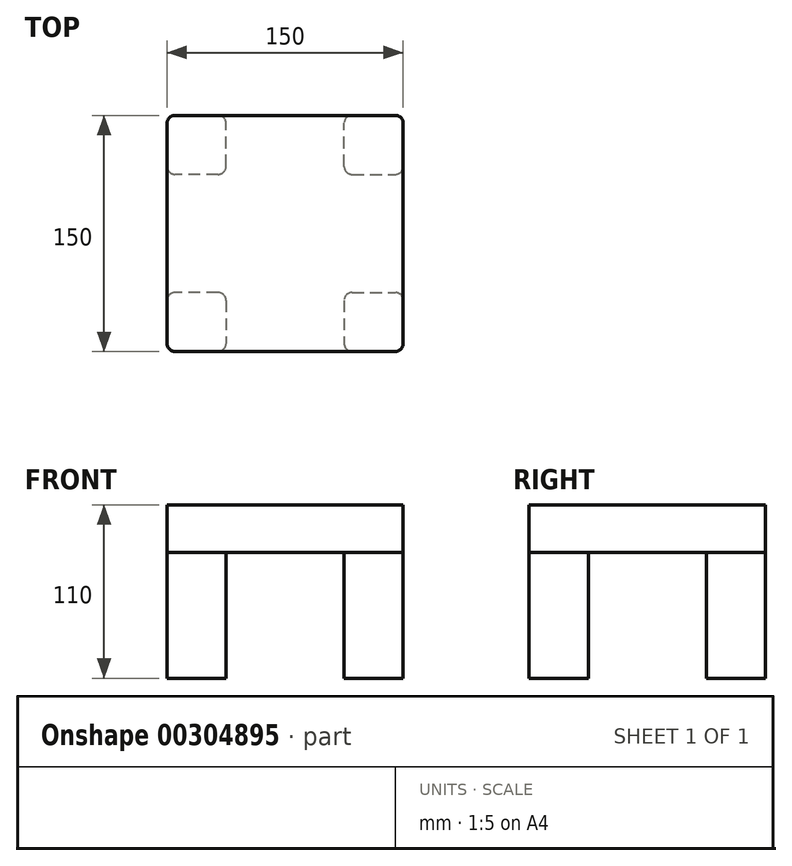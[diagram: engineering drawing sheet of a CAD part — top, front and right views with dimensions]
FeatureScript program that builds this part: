
annotation { "Feature Type Name" : "Feature", "Feature Type Description" : "" }
export const myFeature = defineFeature(function(context is Context, id is Id, definition is map)
    precondition{}
    {
        {
            var Q0;
            Q0=qCreatedBy(makeId("Top.planeOp"),FACE);
            var sketch = newSketch(context, id + "F0", { "sketchPlane" : qUnion([Q0])});
            skLineSegment(sketch, "E0.bottom", {"start": v(0, 0) * mm, "end": v(-75, 0) * mm});
            skLineSegment(sketch, "E0.top", {"start": v(0, 0) * mm, "end": v(-75, 0) * mm});
            skLineSegment(sketch, "E0.left", {"start": v(0, 0) * mm, "end": v(0, 0) * mm});
            skLineSegment(sketch, "E0.right", {"start": v(-75, 0) * mm, "end": v(-75, 0) * mm});
            skLineSegment(sketch, "E1", {"start": v(0, 0) * mm, "end": v(0, -75) * mm});
            skPoint(sketch, "E2.firstSnap0", {"position": v(-37.5, 0) * mm});
            skPoint(sketch, "E2.firstSnap1", {"position": v(0, -37.5) * mm});
            skLineSegment(sketch, "E2.bottom", {"start": v(-42.5, -37.5) * mm, "end": v(-70, -37.5) * mm});
            skLineSegment(sketch, "E2.top", {"start": v(-42.5, -75) * mm, "end": v(-70, -75) * mm});
            skLineSegment(sketch, "E2.left", {"start": v(-37.5, -42.5) * mm, "end": v(-37.5, -70) * mm});
            skLineSegment(sketch, "E2.right", {"start": v(-75, -42.5) * mm, "end": v(-75, -70) * mm});
            skLineSegment(sketch, "E3.MirrorCS", {"start": v(42.5, -37.5) * mm, "end": v(70, -37.5) * mm});
            skLineSegment(sketch, "E4.MirrorCS", {"start": v(75, -42.5) * mm, "end": v(75, -70) * mm});
            skLineSegment(sketch, "E5.MirrorCS", {"start": v(42.5, -75) * mm, "end": v(70, -75) * mm});
            skLineSegment(sketch, "E6.MirrorCS", {"start": v(37.5, -42.5) * mm, "end": v(37.5, -70) * mm});
            skLineSegment(sketch, "E7.MirrorCS", {"start": v(0, 0) * mm, "end": v(75, 0) * mm});
            skLineSegment(sketch, "E8.MirrorCS", {"start": v(-42.5, 37.5) * mm, "end": v(-70, 37.5) * mm});
            skLineSegment(sketch, "E9.MirrorCS", {"start": v(-75, 42.5) * mm, "end": v(-75, 70) * mm});
            skLineSegment(sketch, "E10.MirrorCS", {"start": v(-42.5, 75) * mm, "end": v(-70, 75) * mm});
            skLineSegment(sketch, "E11.MirrorCS", {"start": v(-37.5, 42.5) * mm, "end": v(-37.5, 70) * mm});
            skLineSegment(sketch, "E12.MirrorCS", {"start": v(37.5, 42.5) * mm, "end": v(37.5, 70) * mm});
            skLineSegment(sketch, "E13.MirrorCS", {"start": v(42.5, 37.5) * mm, "end": v(70, 37.5) * mm});
            skLineSegment(sketch, "E14.MirrorCS", {"start": v(75, 42.5) * mm, "end": v(75, 70) * mm});
            skLineSegment(sketch, "E15.MirrorCS", {"start": v(42.5, 75) * mm, "end": v(70, 75) * mm});
            skPoint(sketch, "E16.visualSharp", {"position": v(-75, -37.5) * mm});
            skArc(sketch, "E16.filletArc", {"start": v(-70, -37.5) * mm, "mid": v(-73.54, -38.96) * mm, "end": v(-75, -42.5) * mm});
            skPoint(sketch, "E17.visualSharp", {"position": v(-37.5, -37.5) * mm});
            skArc(sketch, "E17.filletArc", {"start": v(-37.5, -42.5) * mm, "mid": v(-38.96, -38.96) * mm, "end": v(-42.5, -37.5) * mm});
            skPoint(sketch, "E18.visualSharp", {"position": v(-75, -75) * mm});
            skArc(sketch, "E18.filletArc", {"start": v(-75, -70) * mm, "mid": v(-73.54, -73.54) * mm, "end": v(-70, -75) * mm});
            skPoint(sketch, "E19.visualSharp", {"position": v(-37.5, -75) * mm});
            skArc(sketch, "E19.filletArc", {"start": v(-42.5, -75) * mm, "mid": v(-38.96, -73.54) * mm, "end": v(-37.5, -70) * mm});
            skPoint(sketch, "E20.visualSharp", {"position": v(37.5, -37.5) * mm});
            skArc(sketch, "E20.filletArc", {"start": v(42.5, -37.5) * mm, "mid": v(38.96, -38.96) * mm, "end": v(37.5, -42.5) * mm});
            skPoint(sketch, "E21.visualSharp", {"position": v(75, -37.5) * mm});
            skArc(sketch, "E21.filletArc", {"start": v(75, -42.5) * mm, "mid": v(73.54, -38.96) * mm, "end": v(70, -37.5) * mm});
            skPoint(sketch, "E22.visualSharp", {"position": v(37.5, -75) * mm});
            skArc(sketch, "E22.filletArc", {"start": v(37.5, -70) * mm, "mid": v(38.96, -73.54) * mm, "end": v(42.5, -75) * mm});
            skPoint(sketch, "E23.visualSharp", {"position": v(75, -75) * mm});
            skArc(sketch, "E23.filletArc", {"start": v(70, -75) * mm, "mid": v(73.54, -73.54) * mm, "end": v(75, -70) * mm});
            skPoint(sketch, "E24.visualSharp", {"position": v(-75, 37.5) * mm});
            skArc(sketch, "E24.filletArc", {"start": v(-75, 42.5) * mm, "mid": v(-73.54, 38.96) * mm, "end": v(-70, 37.5) * mm});
            skPoint(sketch, "E25.visualSharp", {"position": v(-75, 75) * mm});
            skArc(sketch, "E25.filletArc", {"start": v(-70, 75) * mm, "mid": v(-73.54, 73.54) * mm, "end": v(-75, 70) * mm});
            skPoint(sketch, "E26.visualSharp", {"position": v(-37.5, 75) * mm});
            skArc(sketch, "E26.filletArc", {"start": v(-37.5, 70) * mm, "mid": v(-38.96, 73.54) * mm, "end": v(-42.5, 75) * mm});
            skPoint(sketch, "E27.visualSharp", {"position": v(-37.5, 37.5) * mm});
            skArc(sketch, "E27.filletArc", {"start": v(-42.5, 37.5) * mm, "mid": v(-38.96, 38.96) * mm, "end": v(-37.5, 42.5) * mm});
            skPoint(sketch, "E28.visualSharp", {"position": v(37.5, 37.5) * mm});
            skArc(sketch, "E28.filletArc", {"start": v(37.5, 42.5) * mm, "mid": v(38.96, 38.96) * mm, "end": v(42.5, 37.5) * mm});
            skPoint(sketch, "E29.visualSharp", {"position": v(37.5, 75) * mm});
            skArc(sketch, "E29.filletArc", {"start": v(42.5, 75) * mm, "mid": v(38.96, 73.54) * mm, "end": v(37.5, 70) * mm});
            skPoint(sketch, "E30.visualSharp", {"position": v(75, 75) * mm});
            skArc(sketch, "E30.filletArc", {"start": v(75, 70) * mm, "mid": v(73.54, 73.54) * mm, "end": v(70, 75) * mm});
            skPoint(sketch, "E31.visualSharp", {"position": v(75, 37.5) * mm});
            skArc(sketch, "E31.filletArc", {"start": v(70, 37.5) * mm, "mid": v(73.54, 38.96) * mm, "end": v(75, 42.5) * mm});
            skPoint(sketch, "E32.startSnap0", {"position": v(-56.25, -75) * mm});
            skPoint(sketch, "E32.startSnap1", {"position": v(-37.5, -56.25) * mm});
            skLineSegment(sketch, "E33.left", {"start": v(-56.25, -66.25) * mm, "end": v(-56.25, -66.25) * mm});
            skLineSegment(sketch, "E33.right", {"start": v(-43.75, -66.25) * mm, "end": v(-43.75, -66.25) * mm});
            skLineSegment(sketch, "E34.bottom", {"start": v(-56.25, -66.25) * mm, "end": v(-63.75, -66.25) * mm});
            skLineSegment(sketch, "E34.top", {"start": v(-48.75, -46.25) * mm, "end": v(-63.75, -46.25) * mm});
            skLineSegment(sketch, "E34.left", {"start": v(-43.75, -61.25) * mm, "end": v(-43.75, -51.25) * mm});
            skLineSegment(sketch, "E34.right", {"start": v(-68.75, -61.25) * mm, "end": v(-68.75, -51.25) * mm});
            skPoint(sketch, "E34.middle", {"position": v(-56.25, -56.25) * mm});
            skLineSegment(sketch, "E35", {"start": v(-48.75, -66.25) * mm, "end": v(-56.25, -66.25) * mm});
            skPoint(sketch, "E36.visualSharp", {"position": v(-68.75, -46.25) * mm});
            skArc(sketch, "E36.filletArc", {"start": v(-63.75, -46.25) * mm, "mid": v(-67.29, -47.71) * mm, "end": v(-68.75, -51.25) * mm});
            skPoint(sketch, "E37.visualSharp", {"position": v(-43.75, -46.25) * mm});
            skArc(sketch, "E37.filletArc", {"start": v(-43.75, -51.25) * mm, "mid": v(-45.21, -47.71) * mm, "end": v(-48.75, -46.25) * mm});
            skPoint(sketch, "E38.visualSharp", {"position": v(-43.75, -66.25) * mm});
            skArc(sketch, "E38.filletArc", {"start": v(-48.75, -66.25) * mm, "mid": v(-45.21, -64.79) * mm, "end": v(-43.75, -61.25) * mm});
            skPoint(sketch, "E39.visualSharp", {"position": v(-68.75, -66.25) * mm});
            skArc(sketch, "E39.filletArc", {"start": v(-68.75, -61.25) * mm, "mid": v(-67.29, -64.79) * mm, "end": v(-63.75, -66.25) * mm});
            skSolve(sketch);
        }
        {
            var Q0;
            Q0=makeQuery(id+"F0.imprint","IMPRINT",FACE,{"disambiguationData":[TD([[makeQuery(id+"F0.imprint","IMPRINT",EDGE,{"derivedFrom":sQuery(id+"F0.wireOp",EDGE,"E12.MirrorCS")}),-1.0]])]});
            var Q1;
            Q1=makeQuery(id+"F0.imprint","IMPRINT",FACE,{"disambiguationData":[TD([[makeQuery(id+"F0.imprint","IMPRINT",EDGE,{"derivedFrom":sQuery(id+"F0.wireOp",EDGE,"E8.MirrorCS")}),-1.0]])]});
            var Q2;
            Q2=makeQuery(id+"F0.imprint","IMPRINT",FACE,{"disambiguationData":[TD([[makeQuery(id+"F0.imprint","IMPRINT",EDGE,{"derivedFrom":sQuery(id+"F0.wireOp",EDGE,"E2.bottom")}),1.0]])]});
            var Q3;
            Q3=makeQuery(id+"F0.imprint","IMPRINT",FACE,{"disambiguationData":[TD([[makeQuery(id+"F0.imprint","IMPRINT",EDGE,{"derivedFrom":sQuery(id+"F0.wireOp",EDGE,"E34.bottom")}),-1.0]])]});
            var Q4;
            Q4=makeQuery(id+"F0.imprint","IMPRINT",FACE,{"disambiguationData":[TD([[makeQuery(id+"F0.imprint","IMPRINT",EDGE,{"derivedFrom":sQuery(id+"F0.wireOp",EDGE,"E3.MirrorCS")}),-1.0]])]});
            extrude(context, id + "F1", {"entities" : qUnion([Q0, Q1, Q2, Q3, Q4]), "depth" : 80 * mm});
        }
        {
            var Q0;
            Q0=makeQuery(id+"F1.opExtrude","CAP_FACE",FACE,{"disambiguationData":[OSD([sQuery(id+"F0.wireOp",EDGE,"E8.MirrorCS"),sQuery(id+"F0.wireOp",EDGE,"E9.MirrorCS"),sQuery(id+"F0.wireOp",EDGE,"E10.MirrorCS"),sQuery(id+"F0.wireOp",EDGE,"E11.MirrorCS"),sQuery(id+"F0.wireOp",EDGE,"E24.filletArc"),sQuery(id+"F0.wireOp",EDGE,"E25.filletArc"),sQuery(id+"F0.wireOp",EDGE,"E26.filletArc"),sQuery(id+"F0.wireOp",EDGE,"E27.filletArc")])],"isStart":false});
            var sketch = newSketch(context, id + "F2", { "sketchPlane" : qUnion([Q0])});
            skLineSegment(sketch, "E40.bottom", {"start": v(-70, 75) * mm, "end": v(70, 75) * mm});
            skLineSegment(sketch, "E40.top", {"start": v(-70, -75) * mm, "end": v(70, -75) * mm});
            skLineSegment(sketch, "E40.left", {"start": v(-75, 70) * mm, "end": v(-75, -70) * mm});
            skLineSegment(sketch, "E40.right", {"start": v(75, 70) * mm, "end": v(75, -70) * mm});
            skPoint(sketch, "E40.middle", {"position": v(0, 0) * mm});
            skPoint(sketch, "E41.visualSharp", {"position": v(-75, 75) * mm});
            skArc(sketch, "E41.filletArc", {"start": v(-70, 75) * mm, "mid": v(-73.54, 73.54) * mm, "end": v(-75, 70) * mm});
            skPoint(sketch, "E42.visualSharp", {"position": v(75, 75) * mm});
            skArc(sketch, "E42.filletArc", {"start": v(75, 70) * mm, "mid": v(73.54, 73.54) * mm, "end": v(70, 75) * mm});
            skPoint(sketch, "E43.visualSharp", {"position": v(75, -75) * mm});
            skArc(sketch, "E43.filletArc", {"start": v(70, -75) * mm, "mid": v(73.54, -73.54) * mm, "end": v(75, -70) * mm});
            skPoint(sketch, "E44.visualSharp", {"position": v(-75, -75) * mm});
            skArc(sketch, "E44.filletArc", {"start": v(-75, -70) * mm, "mid": v(-73.54, -73.54) * mm, "end": v(-70, -75) * mm});
            skSolve(sketch);
        }
        {
            var Q0;
            Q0=makeQuery(id+"F2.imprint","IMPRINT",FACE,{"disambiguationData":[TD([[makeQuery(id+"F2.imprint","IMPRINT",EDGE,{"derivedFrom":sQuery(id+"F2.wireOp",EDGE,"E40.top")}),1.0]])]});
            var Q1;
            {var subQ2=sQuery(id+"F2.wireOp",EDGE,"E41.filletArc");Q1=makeQuery(id+"F2.imprint","IMPRINT",FACE,{"disambiguationData":[TD([[makeQuery(id+"F2.imprint","IMPRINT",EDGE,{"derivedFrom":subQ2}),1.0]])]});}
            extrude(context, id + "F3", {"entities" : qUnion([Q0, Q1]), "depth" : 30 * mm});
        }
    });
